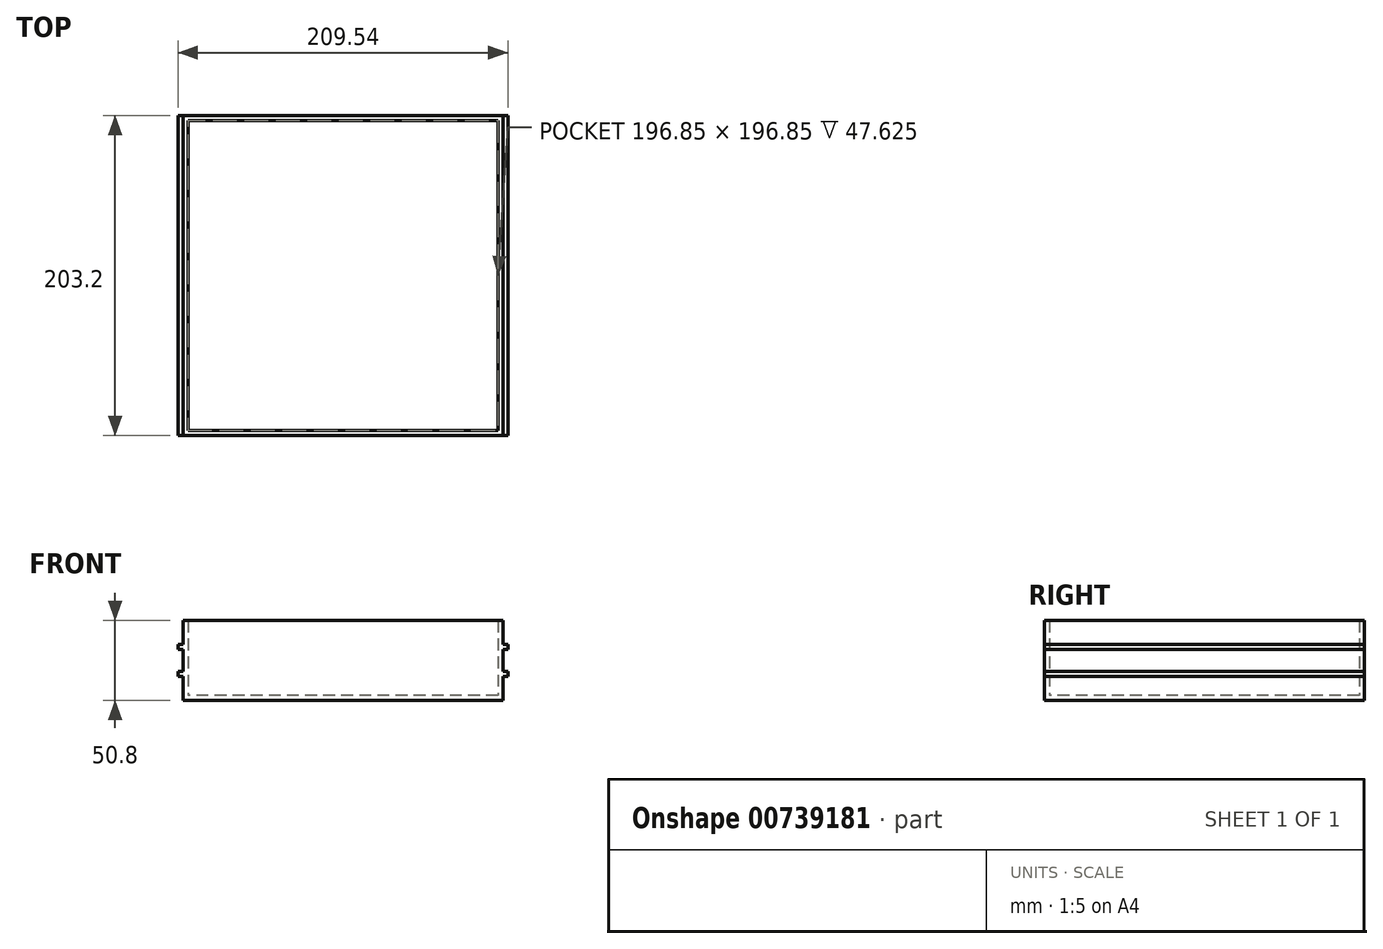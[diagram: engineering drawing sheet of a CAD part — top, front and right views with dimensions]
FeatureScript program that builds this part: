
annotation { "Feature Type Name" : "Feature", "Feature Type Description" : "" }
export const myFeature = defineFeature(function(context is Context, id is Id, definition is map)
    precondition{}
    {
        {
            var Q0;
            Q0=qCreatedBy(makeId("Top.planeOp"),FACE);
            var sketch = newSketch(context, id + "F0", { "sketchPlane" : qUnion([Q0])});
            skLineSegment(sketch, "E0.bottom", {"start": v(101.6, 101.6) * mm, "end": v(-101.6, 101.6) * mm});
            skLineSegment(sketch, "E0.top", {"start": v(101.6, -101.6) * mm, "end": v(-101.6, -101.6) * mm});
            skLineSegment(sketch, "E0.left", {"start": v(101.6, 101.6) * mm, "end": v(101.6, -101.6) * mm});
            skLineSegment(sketch, "E0.right", {"start": v(-101.6, 101.6) * mm, "end": v(-101.6, -101.6) * mm});
            skPoint(sketch, "E0.middle", {"position": v(0, 0) * mm});
            skLineSegment(sketch, "E1.0", {"start": v(-98.43, 98.43) * mm, "end": v(-98.42, -98.43) * mm});
            skLineSegment(sketch, "E1.1", {"start": v(98.43, 98.43) * mm, "end": v(-98.43, 98.43) * mm});
            skLineSegment(sketch, "E1.2", {"start": v(98.43, 98.43) * mm, "end": v(98.43, -98.43) * mm});
            skLineSegment(sketch, "E1.3", {"start": v(98.43, -98.43) * mm, "end": v(-98.42, -98.43) * mm});
            skSolve(sketch);
        }
        {
            var Q0;
            Q0=makeQuery(id+"F0.imprint","IMPRINT",FACE,{"disambiguationData":[TD([[makeQuery(id+"F0.imprint","IMPRINT",EDGE,{"derivedFrom":sQuery(id+"F0.wireOp",EDGE,"E0.bottom")}),1.0]])]});
            extrude(context, id + "F1", {"entities" : qUnion([Q0]), "depth" : 50.8 * mm, "offsetDistance" : 25.4 * mm});
        }
        {
            var Q0;
            Q0=makeQuery(id+"F0.imprint","IMPRINT",FACE,{"disambiguationData":[TD([[makeQuery(id+"F0.imprint","IMPRINT",EDGE,{"derivedFrom":sQuery(id+"F0.wireOp",EDGE,"E1.0")}),1.0]])]});
            extrude(context, id + "F2", {"entities" : qUnion([Q0]), "operationType" : NewBodyOperationType.ADD, "depth" : 3.17 * mm, "offsetDistance" : 25.4 * mm});
        }
        {
            var Q0;
            Q0=makeQuery(id+"F1.opExtrude","SWEPT_FACE",FACE,{"disambiguationData":[OSD([sQuery(id+"F0.wireOp",EDGE,"E0.left")])]});
            var sketch = newSketch(context, id + "F3", { "sketchPlane" : qUnion([Q0])});
            skLineSegment(sketch, "E2", {"start": v(-101.6, 33.87) * mm, "end": v(101.6, 33.87) * mm});
            skLineSegment(sketch, "E3", {"start": v(-101.6, 16.93) * mm, "end": v(101.6, 16.93) * mm});
            skLineSegment(sketch, "E4.bottom", {"start": v(-101.6, 35.45) * mm, "end": v(101.6, 35.45) * mm});
            skLineSegment(sketch, "E4.top", {"start": v(-101.6, 32.28) * mm, "end": v(101.6, 32.28) * mm});
            skLineSegment(sketch, "E4.left", {"start": v(-101.6, 35.45) * mm, "end": v(-101.6, 32.28) * mm});
            skLineSegment(sketch, "E4.right", {"start": v(101.6, 35.45) * mm, "end": v(101.6, 32.28) * mm});
            skLineSegment(sketch, "E5.bottom", {"start": v(-101.6, 18.52) * mm, "end": v(101.6, 18.52) * mm});
            skLineSegment(sketch, "E5.top", {"start": v(-101.6, 15.35) * mm, "end": v(101.6, 15.35) * mm});
            skLineSegment(sketch, "E5.left", {"start": v(-101.6, 18.52) * mm, "end": v(-101.6, 15.35) * mm});
            skLineSegment(sketch, "E5.right", {"start": v(101.6, 18.52) * mm, "end": v(101.6, 15.35) * mm});
            skLineSegment(sketch, "E6", {"start": v(-101.6, 38.63) * mm, "end": v(101.6, 38.63) * mm});
            skLineSegment(sketch, "E7", {"start": v(-101.6, 12.17) * mm, "end": v(101.6, 12.17) * mm});
            skLineSegment(sketch, "E8", {"start": v(-101.6, 29.1) * mm, "end": v(101.6, 29.1) * mm});
            skLineSegment(sketch, "E9", {"start": v(-101.6, 21.7) * mm, "end": v(101.6, 21.7) * mm});
            skSolve(sketch);
        }
        {
            var Q0;
            Q0=makeQuery(id+"F1.opExtrude","SWEPT_FACE",FACE,{"disambiguationData":[OSD([sQuery(id+"F0.wireOp",EDGE,"E0.right")])]});
            var sketch = newSketch(context, id + "F4", { "sketchPlane" : qUnion([Q0])});
            skLineSegment(sketch, "E10", {"start": v(-101.6, 33.87) * mm, "end": v(101.6, 33.87) * mm});
            skLineSegment(sketch, "E11", {"start": v(-101.6, 16.93) * mm, "end": v(101.6, 16.93) * mm});
            skLineSegment(sketch, "E12.bottom", {"start": v(-101.6, 35.45) * mm, "end": v(101.6, 35.45) * mm});
            skLineSegment(sketch, "E12.top", {"start": v(-101.6, 32.28) * mm, "end": v(101.6, 32.28) * mm});
            skLineSegment(sketch, "E12.left", {"start": v(-101.6, 35.45) * mm, "end": v(-101.6, 32.28) * mm});
            skLineSegment(sketch, "E12.right", {"start": v(101.6, 35.45) * mm, "end": v(101.6, 32.28) * mm});
            skLineSegment(sketch, "E13.bottom", {"start": v(-101.6, 18.52) * mm, "end": v(101.6, 18.52) * mm});
            skLineSegment(sketch, "E13.top", {"start": v(-101.6, 15.35) * mm, "end": v(101.6, 15.35) * mm});
            skLineSegment(sketch, "E13.left", {"start": v(-101.6, 18.52) * mm, "end": v(-101.6, 15.35) * mm});
            skLineSegment(sketch, "E13.right", {"start": v(101.6, 18.52) * mm, "end": v(101.6, 15.35) * mm});
            skLineSegment(sketch, "E14", {"start": v(-101.6, 38.63) * mm, "end": v(101.6, 38.63) * mm});
            skLineSegment(sketch, "E15", {"start": v(-101.6, 12.17) * mm, "end": v(101.6, 12.17) * mm});
            skLineSegment(sketch, "E16", {"start": v(-101.6, 29.1) * mm, "end": v(101.6, 29.1) * mm});
            skLineSegment(sketch, "E17", {"start": v(-101.6, 21.7) * mm, "end": v(101.6, 21.7) * mm});
            skSolve(sketch);
        }
        {
            var Q0;
            Q0 = qSketchRegion(id + "F3", true);
            extrude(context, id + "F5", {"entities" : qUnion([Q0]), "operationType" : NewBodyOperationType.ADD, "depth" : 3.17 * mm, "offsetDistance" : 25.4 * mm});
        }
        {
            var Q0;
            Q0 = qSketchRegion(id + "F4", true);
            extrude(context, id + "F6", {"entities" : qUnion([Q0]), "operationType" : NewBodyOperationType.ADD, "depth" : 3.17 * mm, "offsetDistance" : 25.4 * mm});
        }
    });
